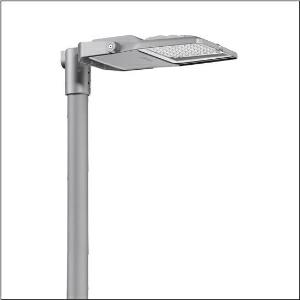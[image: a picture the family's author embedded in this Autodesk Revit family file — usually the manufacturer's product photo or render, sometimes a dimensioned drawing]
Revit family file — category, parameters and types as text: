
# Revit family: floodlight_fl_21_iq_mini___pl43_5xa7772c4a3a_a38e
name_source: partatom
category: Lighting Fixtures
units: mm (PartAtom-declared; Revit-internal decimal feet)

## family parameters
Cut with Voids When Loaded = No
Host = Face
Light Source = No
Part Type = Normal
Room Calculation Point = No
Round Connector Dimension = Use Diameter
Shared = No

## types (1)
- --- (1 x LED, 13050 lm, 87.2 W, 4000K)
    Apparent Load = 87 VA
    CIE Flux Codes = 27 78 99 100 100
    Color Rendering = 70
    Color Temperature = 4000K
    Default Elevation = 1800 mm
    Description = Floodlight FL 21 iQ mini, floodlight, primary light control with lens, of PMMA, primary optical cover: protective disc, of toughened safety glass, transparent, light distribution: PL43, light emission: direct distribution, installation type: surface-mounted, LED, High Power LED, rated luminous flux: 13.050lm, luminous efficacy: 150lm/W, light colour: 740, colour temperature: 4000K, control: Auto-Match, Temp-Guard, Night-Set, Smart-Wire, Desk-Remote (wireless, voltage-free reading and setting of iQ features in the workshop via application-optimized NFC function/RFID function), optimised constant luminous flux control (CLO 2.0), Light-Fading, Lumen-Switch, with terminal, 6-pole, mains connection: 220..240V, AC, 50/60Hz, start of lifetime: 87W, end of service life: 92W, reduction: 40W, luminaire housing, of diecast aluminium, powder-coated, Siteco® metallic grey (DB 702S), corrosivity category C5 mid according to DIN EN ISO 12944, sealing non-destructively replaceable, please order mast flange separately, mast bracket, of steel, galvanised, powder-coated, protection rating (complete): IP66, insulation class (complete): insulation class II (safety insulation), certification: CE, ENEC, VDE, protection symbol: D, impact resistance: IK08, permissible operating ambient temperature: -40..+40°C, permissible operating ambient temperature for outdoor applications: -40..+50°C, standard: DIN EN 12944, LABS conformity tested according to VDMA 24364:2018-05, packaging unit: 1 piece

Light Distribution: PL43
    Height = 70 mm
    Lamp = 1 x LED
    Lamp Light Flux = 13050 lm
    Lamp Power = 87.2 W
    Lamp count = 1
    Length = 485 mm
    Luminous efficacy = 150 lm/W
    Manufacturer = Siteco
    ModVariant = No
    Model = 5XA7772C4A3A
    Number of Poles = 1
    OnlyDefault = Yes
    Power Factor = 1
    Product Name = Floodlight FL 21 iQ mini | PL43
    Product group = floodlight | pylon annexe
    ProductGroupID = 6200
    Protection Class = Protection class II
    Protection Degree = IP 66
    RLX_Detail_Level = 1
    RLX_Emergency_Light_Flux = 0 lm
    RLX_Emergency_Type = 0
    RLX_Emergency_Type_DB = No
    RlxData = <blob elided: 101317 chars, md5=d2eb0070>
    Socket = socket
    Standby Power = 0 W
    System Light Flux = 13050 lm
    System Power = 87 W
    Type Comments = factory setting: luminous flux: 100 % | dim-lin: 254 | 456 mA
    Type Image = l_1007125.jpg
    URL = http://relux.com
    VarID = @adj_094461
    Voltage = 0 V
    Weight = 0.00 kg
    Width = 337 mm

## geometry (parser evidence)
native form markers: Blend x4, Sweep x11
no freeform markers — native parametric forms only
